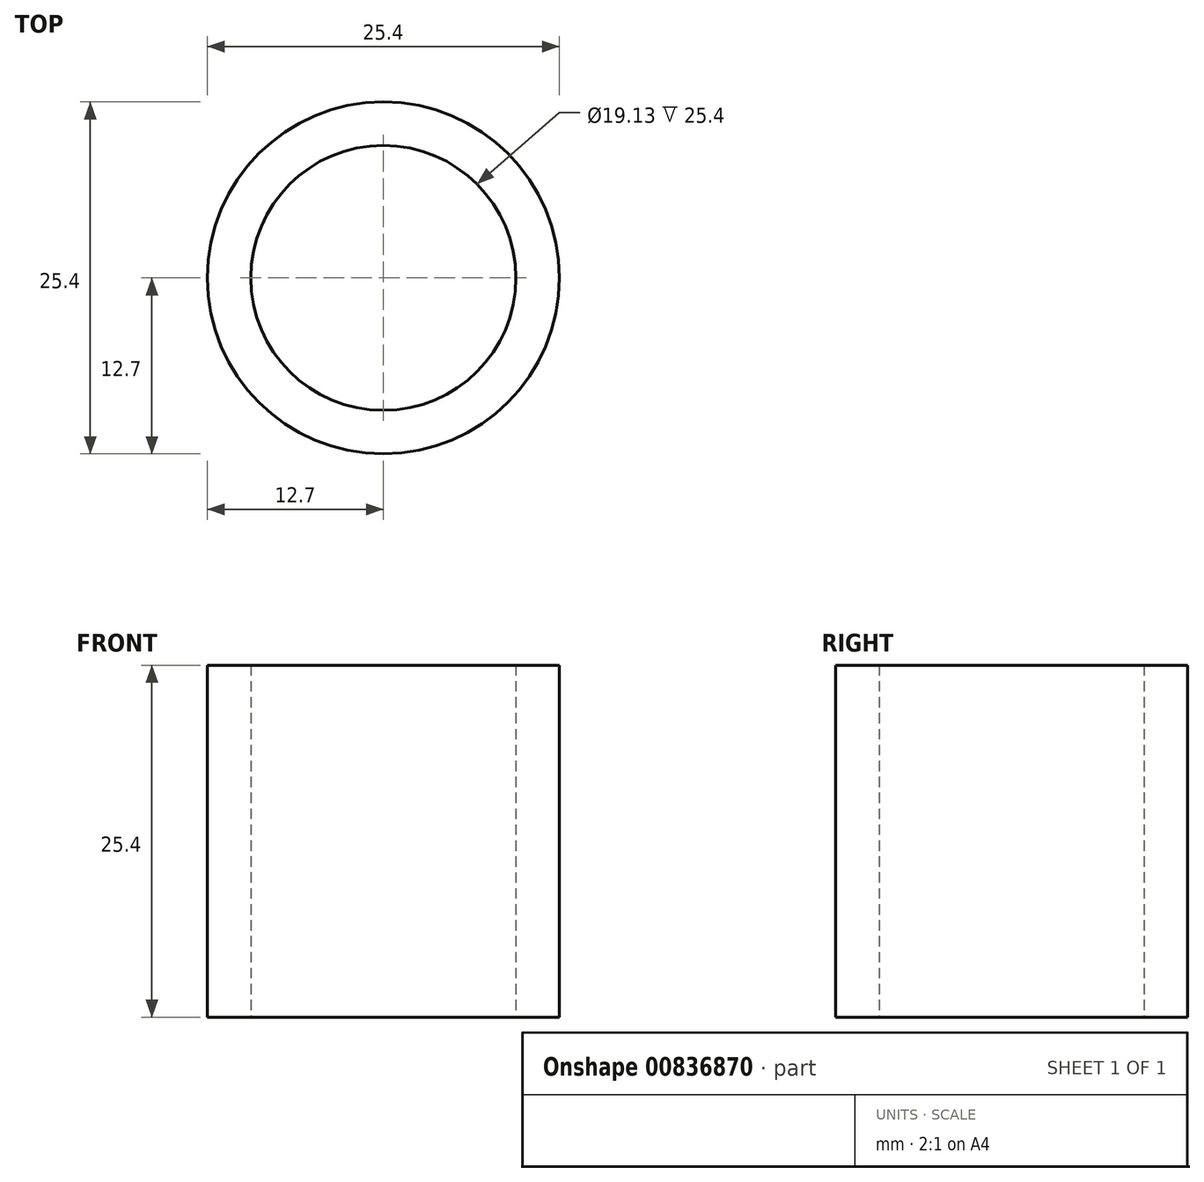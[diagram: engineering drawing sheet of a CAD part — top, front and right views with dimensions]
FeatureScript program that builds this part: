
annotation { "Feature Type Name" : "Feature", "Feature Type Description" : "" }
export const myFeature = defineFeature(function(context is Context, id is Id, definition is map)
    precondition{}
    {
        {
            var Q0;
            Q0=qCreatedBy(makeId("Top.planeOp"),FACE);
            var sketch = newSketch(context, id + "F0", { "sketchPlane" : qUnion([Q0])});
            skCircle(sketch, "E0", {"center": v(0, 0) * mm, "radius": 12.7 * mm});
            skCircle(sketch, "E1", {"center": v(0, 0) * mm, "radius": 9.56 * mm});
            skSolve(sketch);
        }
        {
            var Q0;
            Q0=makeQuery(id+"F0.imprint","IMPRINT",FACE,{"disambiguationData":[TD([[makeQuery(id+"F0.imprint","IMPRINT",EDGE,{"derivedFrom":sQuery(id+"F0.wireOp",EDGE,"E0")}),1.0]])]});
            extrude(context, id + "F1", {"entities" : qUnion([Q0]), "depth" : 25.4 * mm, "offsetDistance" : 25.4 * mm});
        }
    });
